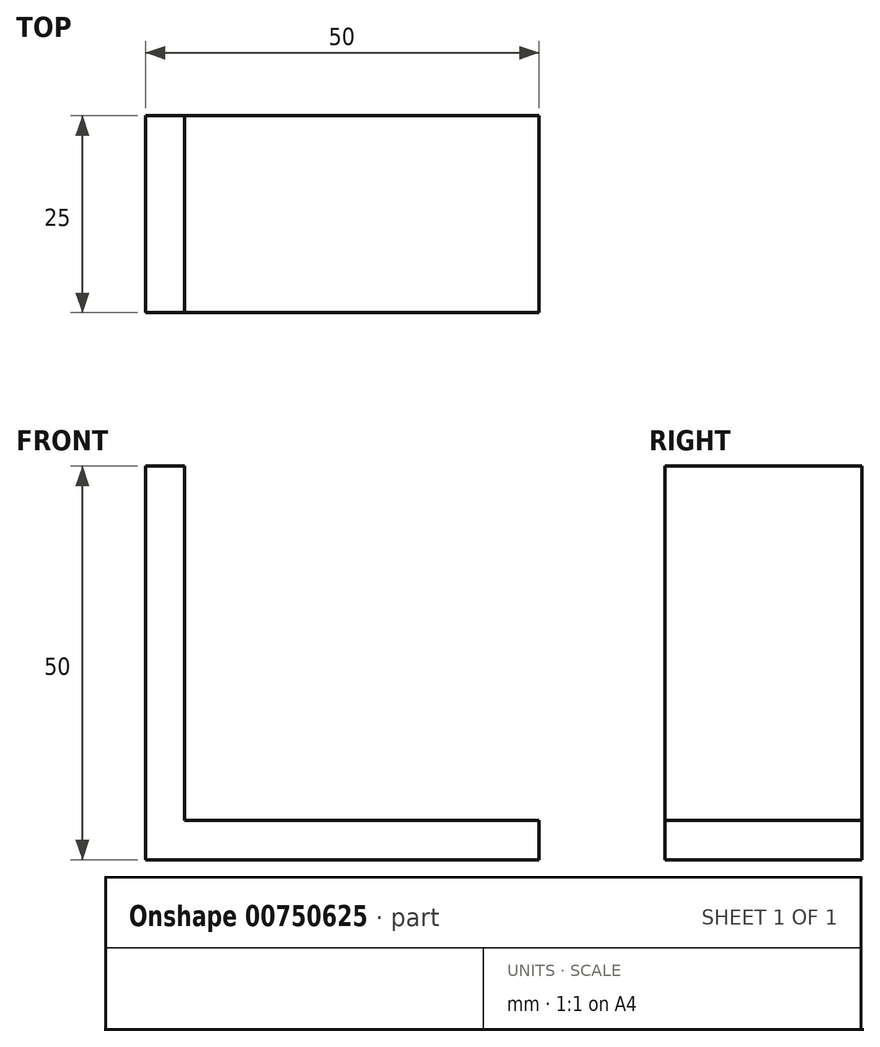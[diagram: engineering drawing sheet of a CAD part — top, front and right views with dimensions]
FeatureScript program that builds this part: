
annotation { "Feature Type Name" : "Feature", "Feature Type Description" : "" }
export const myFeature = defineFeature(function(context is Context, id is Id, definition is map)
    precondition{}
    {
        {
            var Q0;
            Q0=qCreatedBy(makeId("Front.planeOp"),FACE);
            var sketch = newSketch(context, id + "F0", { "sketchPlane" : qUnion([Q0])});
            skLineSegment(sketch, "E0", {"start": v(0, 0) * mm, "end": v(0, 50) * mm});
            skLineSegment(sketch, "E1", {"start": v(0, 50) * mm, "end": v(5, 50) * mm});
            skLineSegment(sketch, "E2", {"start": v(5, 50) * mm, "end": v(5, 5) * mm});
            skLineSegment(sketch, "E3", {"start": v(5, 5) * mm, "end": v(50, 5) * mm});
            skLineSegment(sketch, "E4", {"start": v(50, 5) * mm, "end": v(50, 0) * mm});
            skLineSegment(sketch, "E5", {"start": v(50, 0) * mm, "end": v(0, 0) * mm});
            skSolve(sketch);
        }
        {
            var Q0;
            Q0=makeQuery(id+"F0.imprint","IMPRINT",FACE,{"disambiguationData":[TD([[makeQuery(id+"F0.imprint","IMPRINT",EDGE,{"derivedFrom":sQuery(id+"F0.wireOp",EDGE,"E0")}),-1.0]])]});
            extrude(context, id + "F1", {"entities" : qUnion([Q0]), "endBound" : BoundingType.SYMMETRIC, "depth" : 25 * mm, "offsetDistance" : 25 * mm});
        }
    });
